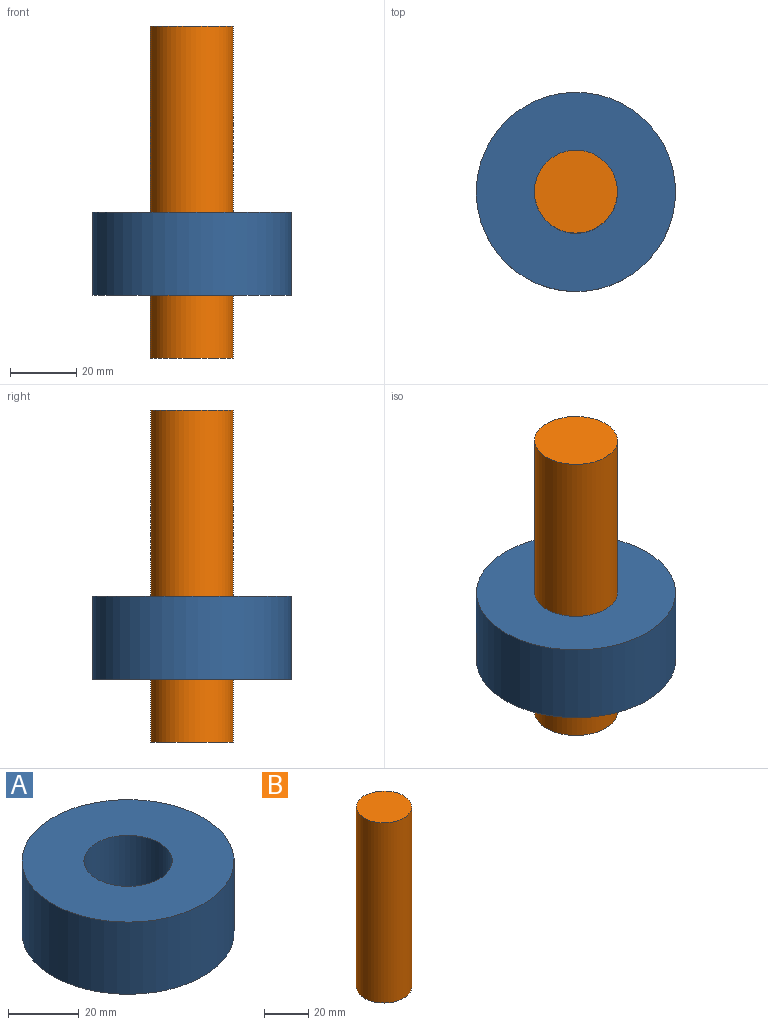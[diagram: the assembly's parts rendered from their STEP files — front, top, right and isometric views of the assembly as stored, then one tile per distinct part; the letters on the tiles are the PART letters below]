
ASSEMBLY  parts=2 mates=1
PART A: 4 faces, bbox 60x60x25 mm
  f0: cylinder r=12.5mm len=25mm, axis (0,0,1), area 1963.5mm2, adj f2,f3
  f1: cylinder r=30mm len=60mm, axis (0,0,1), area 4712.4mm2, adj f2,f3
  f2: plane 60x60mm, normal (0,0,-1), area 2336.6mm2, adj f0,f1
  f3: plane 60x60mm, normal (0,0,1), area 2336.6mm2, adj f0,f1
PART B: 3 faces, bbox 25x25x100 mm
  f0: cylinder r=12.5mm len=100mm, axis (0,0,-1), area 7854mm2, adj f1,f2
  f1: plane 25x25mm, normal (0,0,1), area 490.9mm2, adj f0
  f2: plane 25x25mm, normal (0,0,-1), area 490.9mm2, adj f0
PLACE A t=(13.4,53.61,100.56)mm
PLACE B t=(13.4,53.61,56.63)mm
MATE slider A.f0 <-> B.f0  axis (0,0,1) through (13.4,53.61,100.56)mm
